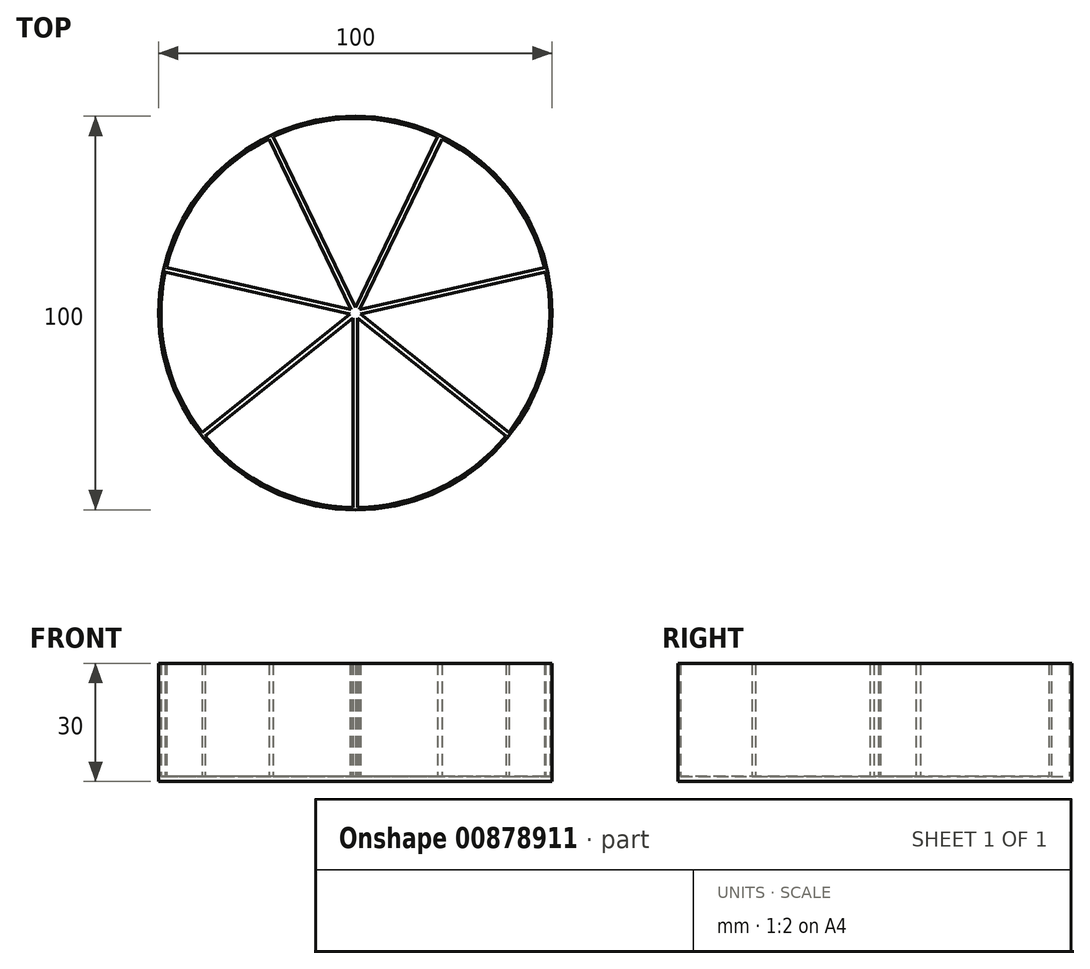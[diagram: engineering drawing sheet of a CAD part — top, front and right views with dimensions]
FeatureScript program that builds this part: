
annotation { "Feature Type Name" : "Feature", "Feature Type Description" : "" }
export const myFeature = defineFeature(function(context is Context, id is Id, definition is map)
    precondition{}
    {
        {
            assignVariable(context, id + "F0", {"name" : "NozzleWidth", "anyValue" : 0.6});
        }
        {
            assignVariable(context, id + "F1", {"name" : "Height", "anyValue" : 30});
        }
        {
            var Q0;
            Q0=qCreatedBy(makeId("Top.planeOp"),FACE);
            var sketch = newSketch(context, id + "F2", { "sketchPlane" : qUnion([Q0])});
            skCircle(sketch, "E0", {"center": v(0, 0) * mm, "radius": 50 * mm});
            skLineSegment(sketch, "E1", {"start": v(0, 0) * mm, "end": v(0, -50) * mm});
            skLineSegment(sketch, "E2.1.0", {"start": v(0, 0) * mm, "end": v(39.1, -31.17) * mm});
            skLineSegment(sketch, "E2.2.0", {"start": v(0, 0) * mm, "end": v(48.75, 11.13) * mm});
            skLineSegment(sketch, "E2.3.0", {"start": v(0, 0) * mm, "end": v(21.7, 45.05) * mm});
            skLineSegment(sketch, "E2.4.0", {"start": v(0, 0) * mm, "end": v(-21.7, 45.05) * mm});
            skLineSegment(sketch, "E2.5.0", {"start": v(0, 0) * mm, "end": v(-48.75, 11.13) * mm});
            skLineSegment(sketch, "E2.6.0", {"start": v(0, 0) * mm, "end": v(-39.1, -31.17) * mm});
            skSolve(sketch);
        }
        {
            var Q0;
            Q0=qCreatedBy(makeId("Top.planeOp"),FACE);
            var sketch = newSketch(context, id + "F3", { "sketchPlane" : qUnion([Q0])});
            skLineSegment(sketch, "E3.0.0", {"start": v(0, 0) * mm, "end": v(-39.1, -31.17) * mm});
            skArc(sketch, "E3.0.1", {"start": v(-39.1, -31.17) * mm, "mid": v(-21.7, -45.05) * mm, "end": v(0, -50) * mm});
            skLineSegment(sketch, "E3.0.2", {"start": v(0, -50) * mm, "end": v(0, 0) * mm, "construction": true});
            skLineSegment(sketch, "E4.0.0", {"start": v(-39.1, -31.17) * mm, "end": v(0, 0) * mm, "construction": true});
            skLineSegment(sketch, "E4.0.1", {"start": v(0, 0) * mm, "end": v(-48.75, 11.13) * mm});
            skArc(sketch, "E4.0.2", {"start": v(-48.75, 11.13) * mm, "mid": v(-48.75, -11.13) * mm, "end": v(-39.1, -31.17) * mm});
            skLineSegment(sketch, "E5.0.0", {"start": v(0, 0) * mm, "end": v(-21.7, 45.05) * mm});
            skArc(sketch, "E5.0.1", {"start": v(-21.7, 45.05) * mm, "mid": v(-39.1, 31.17) * mm, "end": v(-48.75, 11.13) * mm});
            skLineSegment(sketch, "E5.0.2", {"start": v(-48.75, 11.13) * mm, "end": v(0, 0) * mm, "construction": true});
            skLineSegment(sketch, "E6.0.0", {"start": v(-21.7, 45.05) * mm, "end": v(0, 0) * mm, "construction": true});
            skLineSegment(sketch, "E6.0.1", {"start": v(0, 0) * mm, "end": v(21.7, 45.05) * mm, "construction": true});
            skArc(sketch, "E6.0.2", {"start": v(21.7, 45.05) * mm, "mid": v(0, 50) * mm, "end": v(-21.7, 45.05) * mm});
            skLineSegment(sketch, "E7.0.0", {"start": v(0, 0) * mm, "end": v(48.75, 11.13) * mm, "construction": true});
            skArc(sketch, "E7.0.1", {"start": v(48.75, 11.13) * mm, "mid": v(39.1, 31.17) * mm, "end": v(21.7, 45.05) * mm});
            skLineSegment(sketch, "E7.0.2", {"start": v(21.7, 45.05) * mm, "end": v(0, 0) * mm});
            skLineSegment(sketch, "E8.0.0", {"start": v(48.75, 11.13) * mm, "end": v(0, 0) * mm});
            skLineSegment(sketch, "E8.0.1", {"start": v(0, 0) * mm, "end": v(39.1, -31.17) * mm, "construction": true});
            skArc(sketch, "E8.0.2", {"start": v(39.1, -31.17) * mm, "mid": v(48.75, -11.13) * mm, "end": v(48.75, 11.13) * mm});
            skLineSegment(sketch, "E9.0.0", {"start": v(0, 0) * mm, "end": v(0, -50) * mm});
            skArc(sketch, "E9.0.1", {"start": v(0, -50) * mm, "mid": v(21.7, -45.05) * mm, "end": v(39.1, -31.17) * mm});
            skLineSegment(sketch, "E9.0.2", {"start": v(39.1, -31.17) * mm, "end": v(0, 0) * mm});
            skLineSegment(sketch, "E10.0", {"start": v(-0.6, -1.25) * mm, "end": v(-38.25, -31.27) * mm});
            skLineSegment(sketch, "E10.1", {"start": v(-0.6, -49.4) * mm, "end": v(-0.6, -1.25) * mm});
            skArc(sketch, "E10.2", {"start": v(-38.25, -31.27) * mm, "mid": v(-21.43, -44.5) * mm, "end": v(-0.6, -49.4) * mm});
            skLineSegment(sketch, "E11.0", {"start": v(0.6, -1.25) * mm, "end": v(0.6, -49.4) * mm});
            skLineSegment(sketch, "E11.1", {"start": v(38.25, -31.27) * mm, "end": v(0.6, -1.25) * mm});
            skArc(sketch, "E11.2", {"start": v(0.6, -49.4) * mm, "mid": v(21.43, -44.5) * mm, "end": v(38.25, -31.27) * mm});
            skLineSegment(sketch, "E12.0", {"start": v(48.3, 10.4) * mm, "end": v(1.35, -0.3) * mm});
            skArc(sketch, "E12.1", {"start": v(39, -30.33) * mm, "mid": v(48.16, -11) * mm, "end": v(48.3, 10.4) * mm});
            skLineSegment(sketch, "E12.2", {"start": v(1.35, -0.3) * mm, "end": v(39, -30.33) * mm});
            skLineSegment(sketch, "E13.0", {"start": v(-20.9, 44.76) * mm, "end": v(0, 1.38) * mm});
            skArc(sketch, "E13.1", {"start": v(20.9, 44.76) * mm, "mid": v(0, 49.4) * mm, "end": v(-20.9, 44.76) * mm});
            skLineSegment(sketch, "E13.2", {"start": v(0, 1.38) * mm, "end": v(20.9, 44.76) * mm});
            skLineSegment(sketch, "E14.0", {"start": v(1.08, 0.86) * mm, "end": v(48.02, 11.58) * mm});
            skLineSegment(sketch, "E14.1", {"start": v(21.97, 44.24) * mm, "end": v(1.08, 0.86) * mm});
            skArc(sketch, "E14.2", {"start": v(48.02, 11.58) * mm, "mid": v(38.62, 30.8) * mm, "end": v(21.97, 44.24) * mm});
            skLineSegment(sketch, "E15.0", {"start": v(-1.08, 0.86) * mm, "end": v(-21.97, 44.24) * mm});
            skLineSegment(sketch, "E15.1", {"start": v(-48.02, 11.58) * mm, "end": v(-1.08, 0.86) * mm});
            skArc(sketch, "E15.2", {"start": v(-21.97, 44.24) * mm, "mid": v(-38.62, 30.8) * mm, "end": v(-48.02, 11.58) * mm});
            skLineSegment(sketch, "E16.0", {"start": v(-39, -30.33) * mm, "end": v(-1.35, -0.3) * mm});
            skArc(sketch, "E16.1", {"start": v(-48.3, 10.4) * mm, "mid": v(-48.16, -11) * mm, "end": v(-39, -30.33) * mm});
            skLineSegment(sketch, "E16.2", {"start": v(-1.35, -0.3) * mm, "end": v(-48.3, 10.4) * mm});
            skSolve(sketch);
        }
        {
            var Q0;
            Q0=makeQuery(id+"F3.imprint","IMPRINT",FACE,{"disambiguationData":[TD([[makeQuery(id+"F3.imprint","IMPRINT",EDGE,{"derivedFrom":sQuery(id+"F3.wireOp",EDGE,"E3.0.0")}),1.0]])]});
            var Q1;
            Q1=makeQuery(id+"F3.imprint","IMPRINT",FACE,{"disambiguationData":[TD([[makeQuery(id+"F3.imprint","IMPRINT",EDGE,{"derivedFrom":sQuery(id+"F3.wireOp",EDGE,"E9.0.0")}),1.0]])]});
            var Q2;
            Q2=makeQuery(id+"F3.imprint","IMPRINT",FACE,{"disambiguationData":[TD([[makeQuery(id+"F3.imprint","IMPRINT",EDGE,{"derivedFrom":sQuery(id+"F3.wireOp",EDGE,"E3.0.0")}),-1.0]])]});
            var Q3;
            Q3=makeQuery(id+"F3.imprint","IMPRINT",FACE,{"disambiguationData":[TD([[makeQuery(id+"F3.imprint","IMPRINT",EDGE,{"derivedFrom":sQuery(id+"F3.wireOp",EDGE,"E4.0.1")}),-1.0]])]});
            var Q4;
            Q4=makeQuery(id+"F3.imprint","IMPRINT",FACE,{"disambiguationData":[TD([[makeQuery(id+"F3.imprint","IMPRINT",EDGE,{"derivedFrom":sQuery(id+"F3.wireOp",EDGE,"E5.0.0")}),-1.0]])]});
            var Q5;
            Q5=makeQuery(id+"F3.imprint","IMPRINT",FACE,{"disambiguationData":[TD([[makeQuery(id+"F3.imprint","IMPRINT",EDGE,{"derivedFrom":sQuery(id+"F3.wireOp",EDGE,"E7.0.1")}),1.0]])]});
            var Q6;
            Q6=makeQuery(id+"F3.imprint","IMPRINT",FACE,{"disambiguationData":[TD([[makeQuery(id+"F3.imprint","IMPRINT",EDGE,{"derivedFrom":sQuery(id+"F3.wireOp",EDGE,"E8.0.0")}),1.0]])]});
            extrude(context, id + "F4", {"entities" : qUnion([Q0, Q1, Q2, Q3, Q4, Q5, Q6]), "depth" : (getVariable(context, 'Height')) * mm, "offsetDistance" : 25 * mm});
        }
        {
            var Q0;
            {var subQ0=sQuery(id+"F2.wireOp",EDGE,"E2.5.0");Q0=makeQuery(id+"F2.imprint","IMPRINT",FACE,{"disambiguationData":[TD([[makeQuery(id+"F2.imprint","IMPRINT",EDGE,{"derivedFrom":subQ0}),1.0]])]});}
            var Q1;
            {var subQ0=sQuery(id+"F2.wireOp",EDGE,"E2.4.0");Q1=makeQuery(id+"F2.imprint","IMPRINT",FACE,{"disambiguationData":[TD([[makeQuery(id+"F2.imprint","IMPRINT",EDGE,{"derivedFrom":subQ0}),1.0]])]});}
            var Q2;
            {var subQ0=sQuery(id+"F2.wireOp",EDGE,"E2.3.0");Q2=makeQuery(id+"F2.imprint","IMPRINT",FACE,{"disambiguationData":[TD([[makeQuery(id+"F2.imprint","IMPRINT",EDGE,{"derivedFrom":subQ0}),1.0]])]});}
            var Q3;
            {var subQ0=sQuery(id+"F2.wireOp",EDGE,"E2.2.0");Q3=makeQuery(id+"F2.imprint","IMPRINT",FACE,{"disambiguationData":[TD([[makeQuery(id+"F2.imprint","IMPRINT",EDGE,{"derivedFrom":subQ0}),1.0]])]});}
            var Q4;
            {var subQ0=sQuery(id+"F2.wireOp",EDGE,"E2.1.0");Q4=makeQuery(id+"F2.imprint","IMPRINT",FACE,{"disambiguationData":[TD([[makeQuery(id+"F2.imprint","IMPRINT",EDGE,{"derivedFrom":subQ0}),1.0]])]});}
            var Q5;
            {var subQ0=sQuery(id+"F2.wireOp",EDGE,"E1");Q5=makeQuery(id+"F2.imprint","IMPRINT",FACE,{"disambiguationData":[TD([[makeQuery(id+"F2.imprint","IMPRINT",EDGE,{"derivedFrom":subQ0}),1.0]])]});}
            var Q6;
            {var subQ0=sQuery(id+"F2.wireOp",EDGE,"E1");Q6=makeQuery(id+"F2.imprint","IMPRINT",FACE,{"disambiguationData":[TD([[makeQuery(id+"F2.imprint","IMPRINT",EDGE,{"derivedFrom":subQ0}),-1.0]])]});}
            extrude(context, id + "F5", {"entities" : qUnion([Q0, Q1, Q2, Q3, Q4, Q5, Q6]), "operationType" : NewBodyOperationType.ADD, "depth" : (getVariable(context, 'NozzleWidth') * 2) * mm, "offsetDistance" : 25 * mm});
        }
    });
